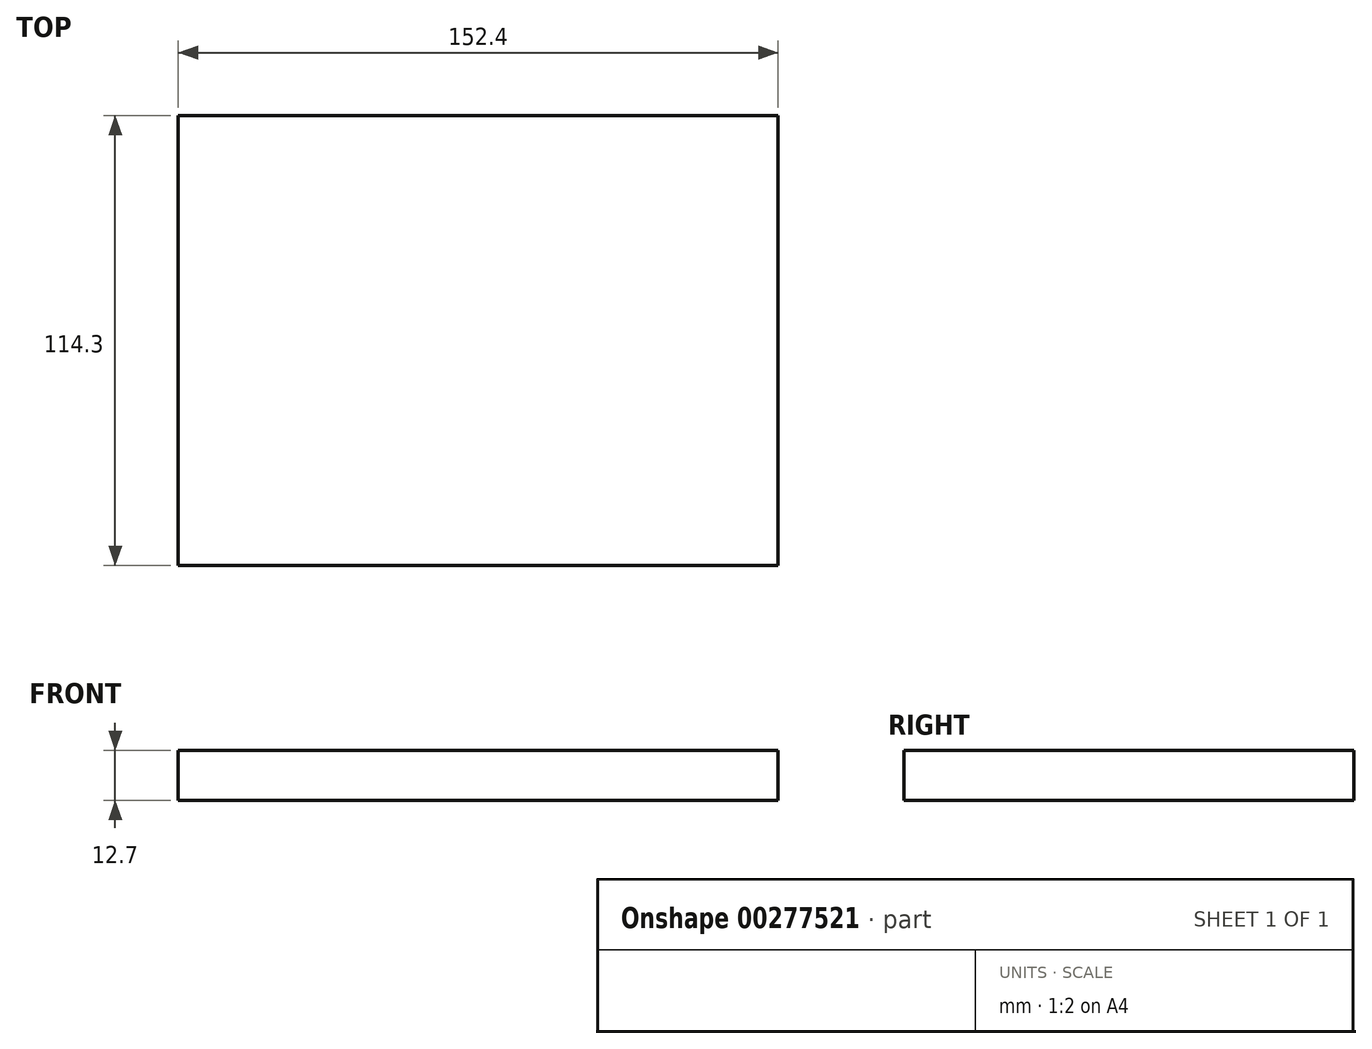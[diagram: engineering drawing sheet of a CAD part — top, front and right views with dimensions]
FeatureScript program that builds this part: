
annotation { "Feature Type Name" : "Feature", "Feature Type Description" : "" }
export const myFeature = defineFeature(function(context is Context, id is Id, definition is map)
    precondition{}
    {
        {
            var Q0;
            Q0=qCreatedBy(makeId("Top.planeOp"),FACE);
            var sketch = newSketch(context, id + "F0", { "sketchPlane" : qUnion([Q0])});
            skLineSegment(sketch, "E0.bottom", {"start": v(-76.2, 57.15) * mm, "end": v(76.2, 57.15) * mm});
            skLineSegment(sketch, "E0.top", {"start": v(-76.2, -57.15) * mm, "end": v(76.2, -57.15) * mm});
            skLineSegment(sketch, "E0.left", {"start": v(-76.2, 57.15) * mm, "end": v(-76.2, -57.15) * mm});
            skLineSegment(sketch, "E0.right", {"start": v(76.2, 57.15) * mm, "end": v(76.2, -57.15) * mm});
            skPoint(sketch, "E0.middle", {"position": v(0, 0) * mm});
            skSolve(sketch);
        }
        {
            var Q0;
            Q0=makeQuery(id+"F0.imprint","IMPRINT",FACE,{"disambiguationData":[TD([[makeQuery(id+"F0.imprint","IMPRINT",EDGE,{"derivedFrom":sQuery(id+"F0.wireOp",EDGE,"E0.bottom")}),-1.0]])]});
            extrude(context, id + "F1", {"entities" : qUnion([Q0]), "depth" : 12.7 * mm});
        }
    });
